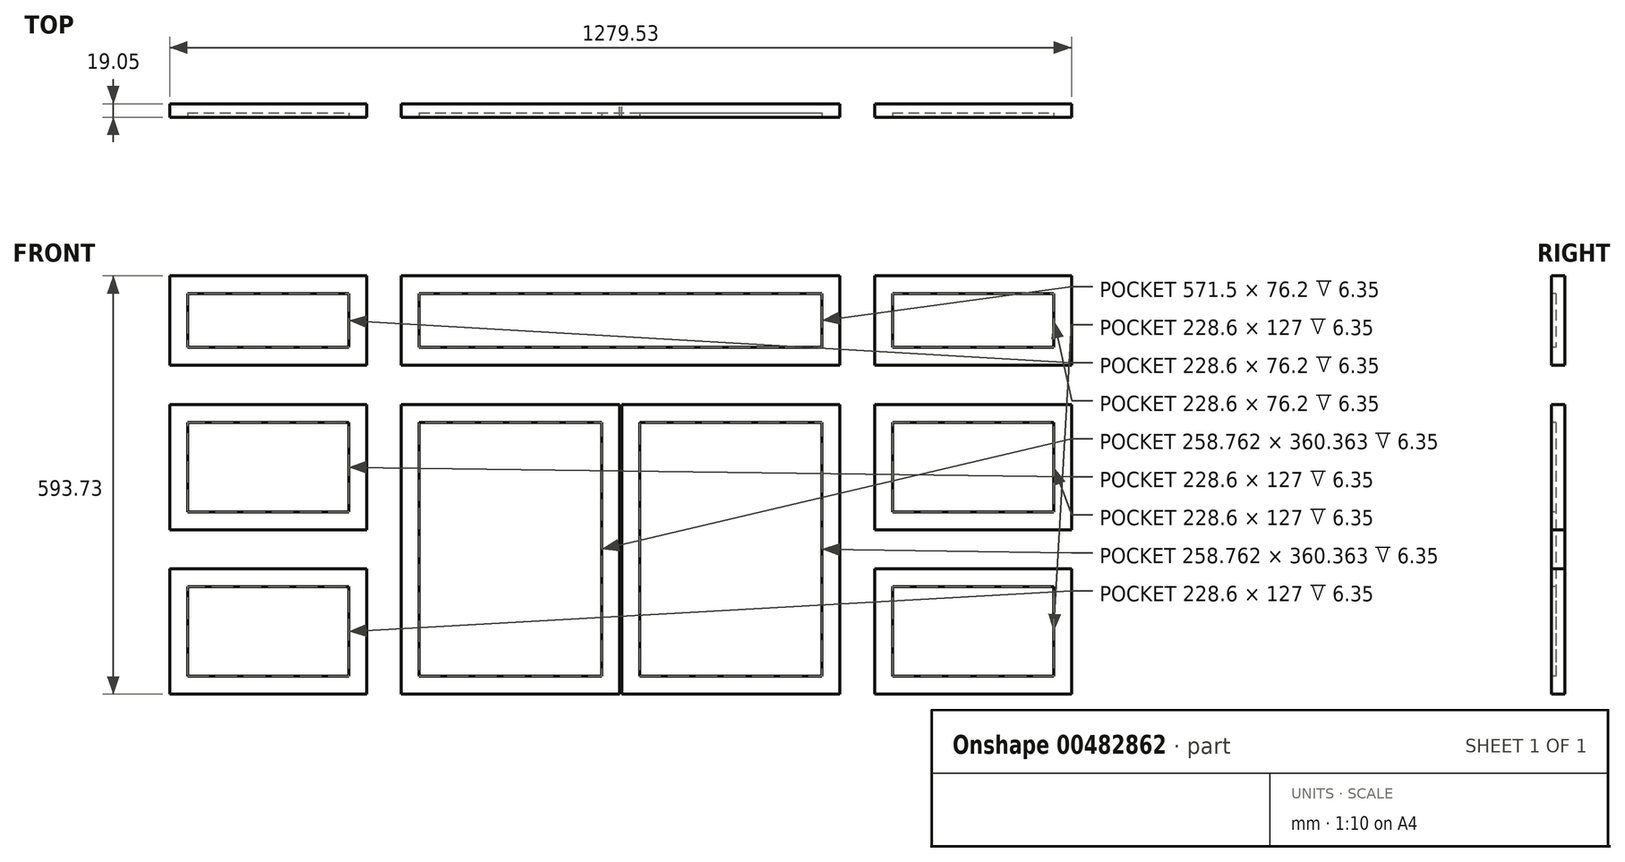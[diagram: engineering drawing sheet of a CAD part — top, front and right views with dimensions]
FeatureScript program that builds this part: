
annotation { "Feature Type Name" : "Feature", "Feature Type Description" : "" }
export const myFeature = defineFeature(function(context is Context, id is Id, definition is map)
    precondition{}
    {
        {
            var Q0;
            Q0=qCreatedBy(makeId("Front.planeOp"),FACE);
            var sketch = newSketch(context, id + "F0", { "sketchPlane" : qUnion([Q0])});
            skPoint(sketch, "E0.middle", {"position": v(0, 0) * mm});
            skLineSegment(sketch, "E1.bottom", {"start": v(-663.58, 266.7) * mm, "end": v(-384.18, 266.7) * mm});
            skLineSegment(sketch, "E1.top", {"start": v(-663.58, 139.7) * mm, "end": v(-384.18, 139.7) * mm});
            skLineSegment(sketch, "E1.left", {"start": v(-663.58, 266.7) * mm, "end": v(-663.58, 139.7) * mm});
            skLineSegment(sketch, "E1.right", {"start": v(-384.18, 266.7) * mm, "end": v(-384.18, 139.7) * mm});
            skLineSegment(sketch, "E2.bottom", {"start": v(-663.58, 84.14) * mm, "end": v(-384.18, 84.14) * mm});
            skLineSegment(sketch, "E2.top", {"start": v(-663.58, -93.66) * mm, "end": v(-384.18, -93.66) * mm});
            skLineSegment(sketch, "E2.left", {"start": v(-663.58, 84.14) * mm, "end": v(-663.58, -93.66) * mm});
            skLineSegment(sketch, "E2.right", {"start": v(-384.18, 84.14) * mm, "end": v(-384.18, -93.66) * mm});
            skLineSegment(sketch, "E3.bottom", {"start": v(-663.58, -149.23) * mm, "end": v(-384.18, -149.23) * mm});
            skLineSegment(sketch, "E3.top", {"start": v(-663.58, -327.03) * mm, "end": v(-384.18, -327.03) * mm});
            skLineSegment(sketch, "E3.left", {"start": v(-663.58, -149.23) * mm, "end": v(-663.58, -327.03) * mm});
            skLineSegment(sketch, "E3.right", {"start": v(-384.18, -149.23) * mm, "end": v(-384.18, -327.03) * mm});
            skLineSegment(sketch, "E4.bottom", {"start": v(-334.96, 266.7) * mm, "end": v(287.34, 266.7) * mm});
            skLineSegment(sketch, "E4.top", {"start": v(-334.96, 139.7) * mm, "end": v(287.34, 139.7) * mm});
            skLineSegment(sketch, "E4.left", {"start": v(-334.96, 266.7) * mm, "end": v(-334.96, 139.7) * mm});
            skLineSegment(sketch, "E4.right", {"start": v(287.34, 266.7) * mm, "end": v(287.34, 139.7) * mm});
            skLineSegment(sketch, "E5.bottom", {"start": v(336.55, 266.7) * mm, "end": v(615.95, 266.7) * mm});
            skLineSegment(sketch, "E5.top", {"start": v(336.55, 139.7) * mm, "end": v(615.95, 139.7) * mm});
            skLineSegment(sketch, "E5.left", {"start": v(336.55, 266.7) * mm, "end": v(336.55, 139.7) * mm});
            skLineSegment(sketch, "E5.right", {"start": v(615.95, 266.7) * mm, "end": v(615.95, 139.7) * mm});
            skLineSegment(sketch, "E6.bottom", {"start": v(336.55, 84.14) * mm, "end": v(615.95, 84.14) * mm});
            skLineSegment(sketch, "E6.top", {"start": v(336.55, -93.66) * mm, "end": v(615.95, -93.66) * mm});
            skLineSegment(sketch, "E6.left", {"start": v(336.55, 84.14) * mm, "end": v(336.55, -93.66) * mm});
            skLineSegment(sketch, "E6.right", {"start": v(615.95, 84.14) * mm, "end": v(615.95, -93.66) * mm});
            skLineSegment(sketch, "E7.bottom", {"start": v(336.55, -149.23) * mm, "end": v(615.95, -149.23) * mm});
            skLineSegment(sketch, "E7.top", {"start": v(336.55, -327.03) * mm, "end": v(615.95, -327.03) * mm});
            skLineSegment(sketch, "E7.left", {"start": v(336.55, -149.22) * mm, "end": v(336.55, -327.02) * mm});
            skLineSegment(sketch, "E7.right", {"start": v(615.95, -149.22) * mm, "end": v(615.95, -327.02) * mm});
            skLineSegment(sketch, "E8.bottom", {"start": v(-334.96, 84.14) * mm, "end": v(-25.4, 84.14) * mm});
            skLineSegment(sketch, "E8.top", {"start": v(-334.96, -327.03) * mm, "end": v(-25.4, -327.03) * mm});
            skLineSegment(sketch, "E8.left", {"start": v(-334.96, 84.14) * mm, "end": v(-334.96, -327.03) * mm});
            skLineSegment(sketch, "E8.right", {"start": v(-25.4, 84.14) * mm, "end": v(-25.4, -327.03) * mm});
            skLineSegment(sketch, "E9.bottom", {"start": v(-22.23, 84.14) * mm, "end": v(287.34, 84.14) * mm});
            skLineSegment(sketch, "E9.top", {"start": v(-22.23, -327.03) * mm, "end": v(287.34, -327.03) * mm});
            skLineSegment(sketch, "E9.left", {"start": v(-22.23, 84.14) * mm, "end": v(-22.23, -327.02) * mm});
            skLineSegment(sketch, "E9.right", {"start": v(287.34, 84.14) * mm, "end": v(287.34, -327.02) * mm});
            skSolve(sketch);
        }
        {
            var Q0;
            Q0=makeQuery(id+"F0.imprint","IMPRINT",FACE,{"disambiguationData":[TD([[makeQuery(id+"F0.imprint","IMPRINT",EDGE,{"derivedFrom":sQuery(id+"F0.wireOp",EDGE,"E1.bottom")}),-1.0]])]});
            var Q1;
            Q1=makeQuery(id+"F0.imprint","IMPRINT",FACE,{"disambiguationData":[TD([[makeQuery(id+"F0.imprint","IMPRINT",EDGE,{"derivedFrom":sQuery(id+"F0.wireOp",EDGE,"E4.bottom")}),-1.0]])]});
            var Q2;
            Q2=makeQuery(id+"F0.imprint","IMPRINT",FACE,{"disambiguationData":[TD([[makeQuery(id+"F0.imprint","IMPRINT",EDGE,{"derivedFrom":sQuery(id+"F0.wireOp",EDGE,"E5.bottom")}),-1.0]])]});
            var Q3;
            Q3=makeQuery(id+"F0.imprint","IMPRINT",FACE,{"disambiguationData":[TD([[makeQuery(id+"F0.imprint","IMPRINT",EDGE,{"derivedFrom":sQuery(id+"F0.wireOp",EDGE,"E6.bottom")}),-1.0]])]});
            var Q4;
            Q4=makeQuery(id+"F0.imprint","IMPRINT",FACE,{"disambiguationData":[TD([[makeQuery(id+"F0.imprint","IMPRINT",EDGE,{"derivedFrom":sQuery(id+"F0.wireOp",EDGE,"E7.bottom")}),-1.0]])]});
            var Q5;
            Q5=makeQuery(id+"F0.imprint","IMPRINT",FACE,{"disambiguationData":[TD([[makeQuery(id+"F0.imprint","IMPRINT",EDGE,{"derivedFrom":sQuery(id+"F0.wireOp",EDGE,"E9.bottom")}),-1.0]])]});
            var Q6;
            Q6=makeQuery(id+"F0.imprint","IMPRINT",FACE,{"disambiguationData":[TD([[makeQuery(id+"F0.imprint","IMPRINT",EDGE,{"derivedFrom":sQuery(id+"F0.wireOp",EDGE,"E8.bottom")}),-1.0]])]});
            var Q7;
            Q7=makeQuery(id+"F0.imprint","IMPRINT",FACE,{"disambiguationData":[TD([[makeQuery(id+"F0.imprint","IMPRINT",EDGE,{"derivedFrom":sQuery(id+"F0.wireOp",EDGE,"E2.bottom")}),-1.0]])]});
            var Q8;
            Q8=makeQuery(id+"F0.imprint","IMPRINT",FACE,{"disambiguationData":[TD([[makeQuery(id+"F0.imprint","IMPRINT",EDGE,{"derivedFrom":sQuery(id+"F0.wireOp",EDGE,"E3.bottom")}),-1.0]])]});
            extrude(context, id + "F1", {"entities" : qUnion([Q0, Q1, Q2, Q3, Q4, Q5, Q6, Q7, Q8]), "depth" : 19.05 * mm});
        }
        {
            var Q0;
            Q0=makeQuery(id+"F1.opExtrude","CAP_FACE",FACE,{"disambiguationData":[OSD([sQuery(id+"F0.wireOp",EDGE,"E2.bottom"),sQuery(id+"F0.wireOp",EDGE,"E2.top"),sQuery(id+"F0.wireOp",EDGE,"E2.left"),sQuery(id+"F0.wireOp",EDGE,"E2.right")])],"isStart":false});
            var sketch = newSketch(context, id + "F2", { "sketchPlane" : qUnion([Q0])});
            skLineSegment(sketch, "E10.bottom", {"start": v(-638.18, 241.3) * mm, "end": v(-409.57, 241.3) * mm});
            skLineSegment(sketch, "E10.top", {"start": v(-638.18, 165.1) * mm, "end": v(-409.57, 165.1) * mm});
            skLineSegment(sketch, "E10.left", {"start": v(-638.18, 241.3) * mm, "end": v(-638.18, 165.1) * mm});
            skLineSegment(sketch, "E10.right", {"start": v(-409.57, 241.3) * mm, "end": v(-409.57, 165.1) * mm});
            skLineSegment(sketch, "E11.bottom", {"start": v(-638.18, 58.74) * mm, "end": v(-409.57, 58.74) * mm});
            skLineSegment(sketch, "E11.top", {"start": v(-638.18, -68.26) * mm, "end": v(-409.57, -68.26) * mm});
            skLineSegment(sketch, "E11.left", {"start": v(-638.18, 58.74) * mm, "end": v(-638.18, -68.26) * mm});
            skLineSegment(sketch, "E11.right", {"start": v(-409.57, 58.74) * mm, "end": v(-409.57, -68.26) * mm});
            skLineSegment(sketch, "E12.bottom", {"start": v(-638.18, -174.63) * mm, "end": v(-409.57, -174.63) * mm});
            skLineSegment(sketch, "E12.top", {"start": v(-638.18, -301.63) * mm, "end": v(-409.57, -301.63) * mm});
            skLineSegment(sketch, "E12.left", {"start": v(-638.18, -174.63) * mm, "end": v(-638.18, -301.63) * mm});
            skLineSegment(sketch, "E12.right", {"start": v(-409.57, -174.63) * mm, "end": v(-409.57, -301.63) * mm});
            skLineSegment(sketch, "E13.bottom", {"start": v(-309.56, 58.74) * mm, "end": v(-50.8, 58.74) * mm});
            skLineSegment(sketch, "E13.top", {"start": v(-309.56, -301.63) * mm, "end": v(-50.8, -301.63) * mm});
            skLineSegment(sketch, "E13.left", {"start": v(-309.56, 58.74) * mm, "end": v(-309.56, -301.63) * mm});
            skLineSegment(sketch, "E13.right", {"start": v(-50.8, 58.74) * mm, "end": v(-50.8, -301.63) * mm});
            skLineSegment(sketch, "E14.bottom", {"start": v(-309.56, 241.3) * mm, "end": v(261.94, 241.3) * mm});
            skLineSegment(sketch, "E14.top", {"start": v(-309.56, 165.1) * mm, "end": v(261.94, 165.1) * mm});
            skLineSegment(sketch, "E14.left", {"start": v(-309.56, 241.3) * mm, "end": v(-309.56, 165.1) * mm});
            skLineSegment(sketch, "E14.right", {"start": v(261.94, 241.3) * mm, "end": v(261.94, 165.1) * mm});
            skLineSegment(sketch, "E15.bottom", {"start": v(3.17, 58.74) * mm, "end": v(261.94, 58.74) * mm});
            skLineSegment(sketch, "E15.top", {"start": v(3.17, -301.63) * mm, "end": v(261.94, -301.63) * mm});
            skLineSegment(sketch, "E15.left", {"start": v(3.17, 58.74) * mm, "end": v(3.17, -301.63) * mm});
            skLineSegment(sketch, "E15.right", {"start": v(261.94, 58.74) * mm, "end": v(261.94, -301.63) * mm});
            skLineSegment(sketch, "E16.bottom", {"start": v(361.95, 241.3) * mm, "end": v(590.55, 241.3) * mm});
            skLineSegment(sketch, "E16.top", {"start": v(361.95, 165.1) * mm, "end": v(590.55, 165.1) * mm});
            skLineSegment(sketch, "E16.left", {"start": v(361.95, 241.3) * mm, "end": v(361.95, 165.1) * mm});
            skLineSegment(sketch, "E16.right", {"start": v(590.55, 241.3) * mm, "end": v(590.55, 165.1) * mm});
            skLineSegment(sketch, "E17.bottom", {"start": v(361.95, 58.74) * mm, "end": v(590.55, 58.74) * mm});
            skLineSegment(sketch, "E17.top", {"start": v(361.95, -68.26) * mm, "end": v(590.55, -68.26) * mm});
            skLineSegment(sketch, "E17.left", {"start": v(361.95, 58.74) * mm, "end": v(361.95, -68.26) * mm});
            skLineSegment(sketch, "E17.right", {"start": v(590.55, 58.74) * mm, "end": v(590.55, -68.26) * mm});
            skLineSegment(sketch, "E18.bottom", {"start": v(361.95, -174.63) * mm, "end": v(590.55, -174.63) * mm});
            skLineSegment(sketch, "E18.top", {"start": v(361.95, -301.63) * mm, "end": v(590.55, -301.63) * mm});
            skLineSegment(sketch, "E18.left", {"start": v(361.95, -174.63) * mm, "end": v(361.95, -301.63) * mm});
            skLineSegment(sketch, "E18.right", {"start": v(590.55, -174.63) * mm, "end": v(590.55, -301.63) * mm});
            skSolve(sketch);
        }
        {
            var Q0;
            Q0 = qSketchRegion(id + "F2", true);
            extrude(context, id + "F3", {"entities" : qUnion([Q0]), "operationType" : NewBodyOperationType.REMOVE, "oppositeDirection" : true, "depth" : 6.35 * mm});
        }
    });
